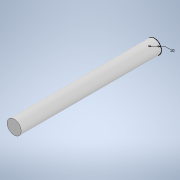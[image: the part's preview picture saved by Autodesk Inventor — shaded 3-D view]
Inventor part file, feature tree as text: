
AUTODESK INVENTOR PART (.ipt)
format: ipt  version: 2021 (Build 250183000, 183)  size: 90,624 bytes
history: native  units: in
note: dims shown in document units (in); Inventor stores cm internally (conversion verified against a paired STEP export)
features: extrude x1, sketch x1
ambient origin geometry x8: Origin, YZ Plane, XZ Plane, XY Plane, X Axis, Y Axis, Z Axis, Center Point
bodies: Body1 (feature_tree)
feature tree (2):
  extrude  "Extrusion2"  Depth=3.937in TaperAngle=0.0deg
  sketch  "Sketch2"  dims[d3=0.3937in d4=3.937in d5=0.0in]
